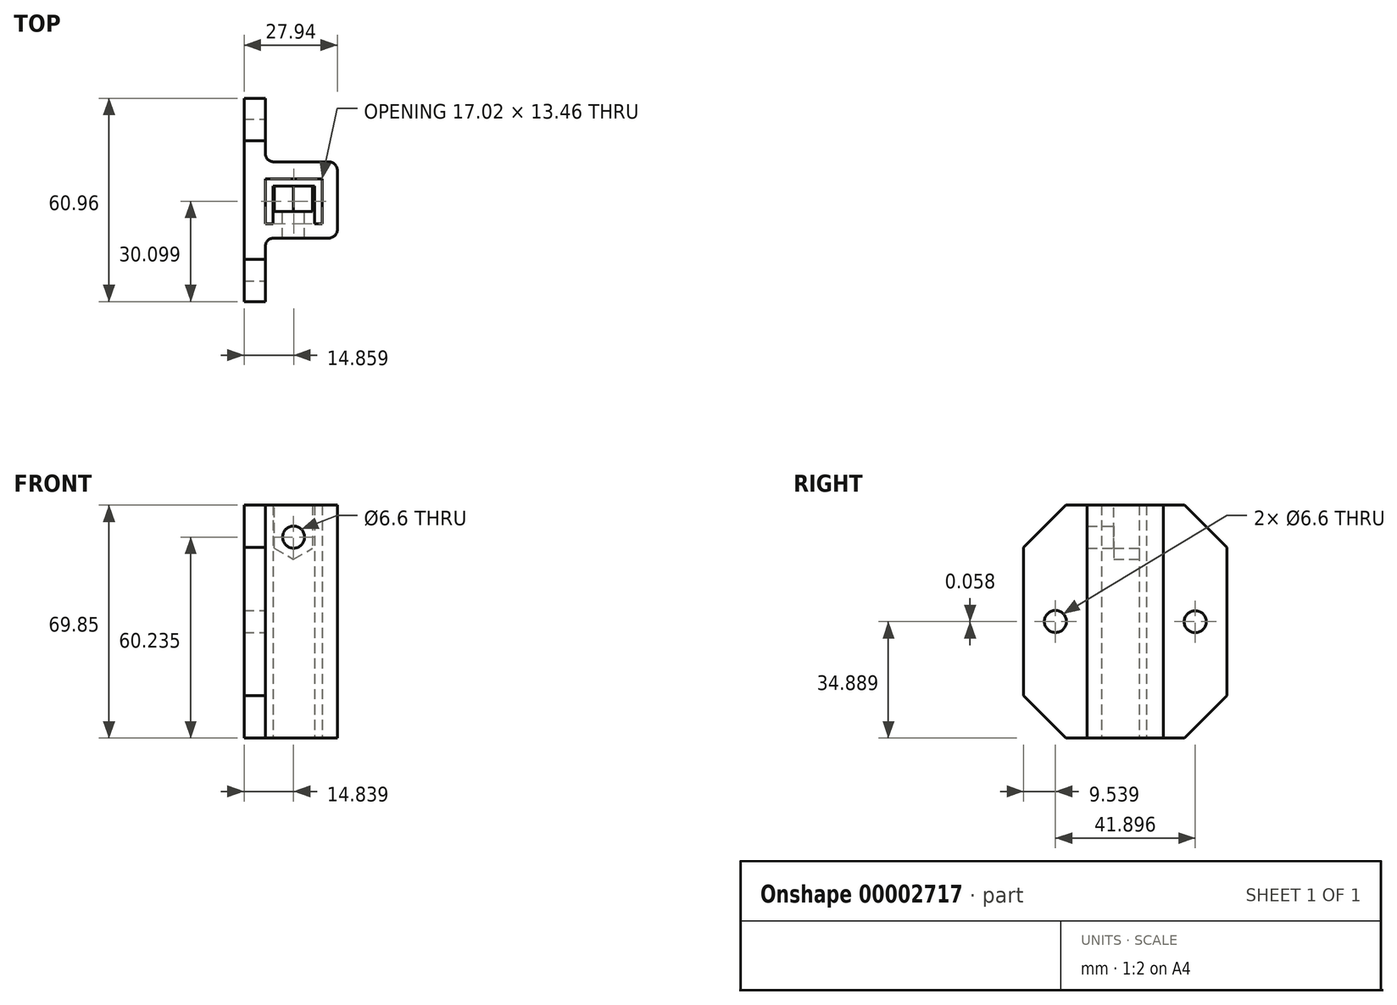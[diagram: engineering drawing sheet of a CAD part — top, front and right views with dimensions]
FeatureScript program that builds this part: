
annotation { "Feature Type Name" : "Feature", "Feature Type Description" : "" }
export const myFeature = defineFeature(function(context is Context, id is Id, definition is map)
    precondition{}
    {
        {
            var Q0;
            Q0=qCreatedBy(makeId("Top.planeOp"),FACE);
            var sketch = newSketch(context, id + "F0", { "sketchPlane" : qUnion([Q0])});
            skLineSegment(sketch, "E0", {"start": v(0, 0) * mm, "end": v(17.02, 0) * mm});
            skLineSegment(sketch, "E1", {"start": v(17.02, 0) * mm, "end": v(17.02, -13.46) * mm});
            skLineSegment(sketch, "E2", {"start": v(17.02, -13.46) * mm, "end": v(14.73, -13.46) * mm});
            skLineSegment(sketch, "E3", {"start": v(14.73, -13.46) * mm, "end": v(14.73, -2.18) * mm});
            skLineSegment(sketch, "E4", {"start": v(14.73, -2.18) * mm, "end": v(2.29, -2.18) * mm});
            skLineSegment(sketch, "E5", {"start": v(2.29, -2.18) * mm, "end": v(2.29, -13.46) * mm});
            skLineSegment(sketch, "E6", {"start": v(2.29, -13.46) * mm, "end": v(0, -13.46) * mm});
            skLineSegment(sketch, "E7", {"start": v(0, -13.46) * mm, "end": v(0, 0) * mm});
            skSolve(sketch);
        }
        {
            var Q0;
            Q0=qCreatedBy(makeId("Top.planeOp"),FACE);
            var sketch = newSketch(context, id + "F1", { "sketchPlane" : qUnion([Q0])});
            skLineSegment(sketch, "E8.bottom", {"start": v(0, 0) * mm, "end": v(26.67, 0) * mm});
            skLineSegment(sketch, "E8.top", {"start": v(0, -22.86) * mm, "end": v(26.67, -22.86) * mm});
            skLineSegment(sketch, "E8.left", {"start": v(0, 0) * mm, "end": v(0, -22.86) * mm});
            skLineSegment(sketch, "E8.right", {"start": v(26.67, 0) * mm, "end": v(26.67, -22.86) * mm});
            skSolve(sketch);
        }
        {
            var Q0;
            Q0=makeQuery(id+"F1.imprint","IMPRINT",FACE,{"disambiguationData":[TD([[makeQuery(id+"F1.imprint","IMPRINT",EDGE,{"derivedFrom":sQuery(id+"F1.wireOp",EDGE,"E8.bottom")}),-1.0]])]});
            extrude(context, id + "F2", {"entities" : qUnion([Q0]), "depth" : 69.85 * mm});
        }
        {
            var Q0;
            Q0=makeQuery(id+"F2.opExtrude","SWEPT_BODY",BODY,{"disambiguationData":[OSD([sQuery(id+"F1.wireOp",EDGE,"E8.bottom"),sQuery(id+"F1.wireOp",EDGE,"E8.top"),sQuery(id+"F1.wireOp",EDGE,"E8.left"),sQuery(id+"F1.wireOp",EDGE,"E8.right")])]});
            transform(context, id + "F3", {"entities" : qUnion([Q0]), "transformType" : TransformType.TRANSLATION_3D, "dx" : 0 * mm, "dy" : 5.08 * mm, "dz" : 0 * mm, "makeCopy" : false});
        }
        {
            var Q0;
            Q0=qCreatedBy(makeId("Top.planeOp"),FACE);
            var sketch = newSketch(context, id + "F4", { "sketchPlane" : qUnion([Q0])});
            skLineSegment(sketch, "E9", {"start": v(0, 0) * mm, "end": v(-5.08, 0) * mm});
            skSolve(sketch);
        }
        {
            var Q0;
            Q0=makeQuery(id+"F2.opExtrude","SWEPT_BODY",BODY,{"disambiguationData":[OSD([sQuery(id+"F1.wireOp",EDGE,"E8.bottom"),sQuery(id+"F1.wireOp",EDGE,"E8.top"),sQuery(id+"F1.wireOp",EDGE,"E8.left"),sQuery(id+"F1.wireOp",EDGE,"E8.right")])]});
            var Q1;
            Q1=sQuery(id+"F4.wireOp",EDGE,"E9");
            transform(context, id + "F5", {"entities" : qUnion([Q0]), "transformType" : TransformType.TRANSLATION_ENTITY, "oppositeDirectionEntity" : false, "transformLine" : qUnion([Q1]), "makeCopy" : false});
        }
        {
            var Q0;
            Q0=makeQuery(id+"F0.imprint","IMPRINT",FACE,{"disambiguationData":[TD([[makeQuery(id+"F0.imprint","IMPRINT",EDGE,{"derivedFrom":sQuery(id+"F0.wireOp",EDGE,"E0")}),-1.0]])]});
            extrude(context, id + "F6", {"entities" : qUnion([Q0]), "operationType" : NewBodyOperationType.REMOVE, "depth" : 71.12 * mm});
        }
        {
            var Q0;
            Q0=qCreatedBy(makeId("Top.planeOp"),FACE);
            var sketch = newSketch(context, id + "F7", { "sketchPlane" : qUnion([Q0])});
            skLineSegment(sketch, "E10", {"start": v(0, 0) * mm, "end": v(0, 24.13) * mm});
            skLineSegment(sketch, "E11", {"start": v(0, 24.13) * mm, "end": v(-6.35, 24.13) * mm});
            skLineSegment(sketch, "E12", {"start": v(-6.35, 24.13) * mm, "end": v(-6.35, -36.83) * mm});
            skLineSegment(sketch, "E13", {"start": v(-6.35, -36.83) * mm, "end": v(0, -36.83) * mm});
            skLineSegment(sketch, "E14", {"start": v(0, -36.83) * mm, "end": v(0, 0) * mm});
            skSolve(sketch);
        }
        {
            var Q0;
            Q0=makeQuery(id+"F7.imprint","IMPRINT",FACE,{"disambiguationData":[TD([[makeQuery(id+"F7.imprint","IMPRINT",EDGE,{"derivedFrom":sQuery(id+"F7.wireOp",EDGE,"E11")}),1.0]])]});
            extrude(context, id + "F8", {"entities" : qUnion([Q0]), "operationType" : NewBodyOperationType.ADD, "depth" : 69.85 * mm});
        }
        {
            var Q0;
            Q0=makeQuery(id+"F8.opExtrude","CAP_EDGE",EDGE,{"disambiguationData":[OSD([sQuery(id+"F7.wireOp",EDGE,"E13")])],"isStart":true});
            var Q1;
            Q1=makeQuery(id+"F8.opExtrude","CAP_EDGE",EDGE,{"disambiguationData":[OSD([sQuery(id+"F7.wireOp",EDGE,"E13")])],"isStart":false});
            var Q2;
            Q2=makeQuery(id+"F8.opExtrude","CAP_EDGE",EDGE,{"disambiguationData":[OSD([sQuery(id+"F7.wireOp",EDGE,"E11")])],"isStart":false});
            var Q3;
            Q3=makeQuery(id+"F8.opExtrude","CAP_EDGE",EDGE,{"disambiguationData":[OSD([sQuery(id+"F7.wireOp",EDGE,"E11")])],"isStart":true});
            chamfer(context, id + "F9", {"entities" : qUnion([Q0, Q1, Q2, Q3]), "width" : 12.7 * mm, "tangentPropagation" : true});
        }
        {
            var Q0;
            Q0=qCreatedBy(makeId("Top.planeOp"),FACE);
            cPlane(context, id + "F10", {"entities" : qUnion([Q0]), "cplaneType" : CPlaneType.OFFSET, "offset" : 34.92 * mm, "width" : 152.4 * mm, "height" : 152.4 * mm});
        }
        {
            var Q0;
            Q0=qCreatedBy(makeId("Right.planeOp"),FACE);
            var sketch = newSketch(context, id + "F11", { "sketchPlane" : qUnion([Q0])});
            skCircle(sketch, "E15", {"center": v(14.6, 34.89) * mm, "radius": 3.3 * mm});
            skCircle(sketch, "E16", {"center": v(-27.3, 34.95) * mm, "radius": 3.3 * mm});
            skLineSegment(sketch, "E17", {"start": v(14.6, 34.89) * mm, "end": v(-27.3, 34.89) * mm});
            skSolve(sketch);
        }
        {
            var Q0;
            {var subQ1=sQuery(id+"F11.wireOp",EDGE,"E15");var subQ2=sQuery(id+"F11.wireOp",EDGE,"E16");Q0=qUnion([makeQuery(id+"F11.imprint","IMPRINT",FACE,{"disambiguationData":[TD([[makeQuery(id+"F11.imprint","IMPRINT",EDGE,{"derivedFrom":subQ1}),1.0]])]}),makeQuery(id+"F11.imprint","IMPRINT",FACE,{"disambiguationData":[TD([[makeQuery(id+"F11.imprint","IMPRINT",EDGE,{"derivedFrom":subQ2}),1.0]])]})]);}
            extrude(context, id + "F12", {"entities" : qUnion([Q0]), "operationType" : NewBodyOperationType.REMOVE, "oppositeDirection" : true, "depth" : 25.4 * mm});
        }
        {
            var Q0;
            Q0=makeQuery(id+"F2.opExtrude","SWEPT_EDGE",EDGE,{"disambiguationData":[OSD([sQuery(id+"F1.wireOp",EDGE,"E8.top"),sQuery(id+"F1.wireOp",EDGE,"E8.right")])]});
            var Q1;
            Q1=makeQuery(id+"F2.opExtrude","SWEPT_EDGE",EDGE,{"disambiguationData":[OSD([sQuery(id+"F1.wireOp",EDGE,"E8.bottom"),sQuery(id+"F1.wireOp",EDGE,"E8.right")])]});
            var Q2;
            Q2=makeQuery(id+"F8.boolean.opBoolean","INTERSECT",EDGE,{"derivedFrom":[makeQuery(id+"F2.opExtrude","SWEPT_FACE",FACE,{"disambiguationData":[OSD([sQuery(id+"F1.wireOp",EDGE,"E8.bottom")])]}),makeQuery(id+"F8.opExtrude","SWEPT_FACE",FACE,{"disambiguationData":[OSD([sQuery(id+"F7.wireOp",EDGE,"E14")])]})]});
            var Q3;
            Q3=makeQuery(id+"F8.boolean.opBoolean","INTERSECT",EDGE,{"derivedFrom":[makeQuery(id+"F2.opExtrude","SWEPT_FACE",FACE,{"disambiguationData":[OSD([sQuery(id+"F1.wireOp",EDGE,"E8.top")])]}),makeQuery(id+"F8.opExtrude","SWEPT_FACE",FACE,{"disambiguationData":[OSD([sQuery(id+"F7.wireOp",EDGE,"E14")])]})]});
            fillet(context, id + "F13", {"entities" : qUnion([Q0, Q1, Q2, Q3]), "radius" : 2.54 * mm, "tangentPropagation" : true, "allowEdgeOverflow" : false});
        }
        {
            var Q0;
            Q0=qCreatedBy(makeId("Front.planeOp"),FACE);
            var sketch = newSketch(context, id + "F14", { "sketchPlane" : qUnion([Q0])});
            skCircle(sketch, "E18", {"center": v(8.49, 60.23) * mm, "radius": 3.3 * mm});
            skSolve(sketch);
        }
        {
            var Q0;
            Q0=makeQuery(id+"F14.imprint","IMPRINT",FACE,{"disambiguationData":[TD([[makeQuery(id+"F14.imprint","IMPRINT",EDGE,{"derivedFrom":sQuery(id+"F14.wireOp",EDGE,"E18")}),1.0]])]});
            extrude(context, id + "F15", {"entities" : qUnion([Q0]), "operationType" : NewBodyOperationType.REMOVE, "depth" : 25.4 * mm});
        }
        {
            var Q0;
            Q0=makeQuery(id+"F6.boolean.opBoolean","COPY",FACE,{"derivedFrom":makeQuery(id+"F6.opExtrude","SWEPT_FACE",FACE,{"disambiguationData":[OSD([sQuery(id+"F0.wireOp",EDGE,"E4")])]})});
            var sketch = newSketch(context, id + "F16", { "sketchPlane" : qUnion([Q0])});
            skLineSegment(sketch, "E19", {"start": v(-8.49, 60.23) * mm, "end": v(-14.2, 60.23) * mm});
            skCircle(sketch, "E20.cCircle", {"center": v(-8.49, 60.23) * mm, "radius": 5.72 * mm, "construction": true});
            skLineSegment(sketch, "E20.0", {"start": v(-14.2, 56.94) * mm, "end": v(-14.2, 63.53) * mm});
            skLineSegment(sketch, "E20.1", {"start": v(-14.2, 63.53) * mm, "end": v(-8.49, 66.83) * mm});
            skLineSegment(sketch, "E20.2", {"start": v(-8.49, 66.83) * mm, "end": v(-2.77, 63.53) * mm});
            skLineSegment(sketch, "E20.3", {"start": v(-2.77, 63.53) * mm, "end": v(-2.77, 56.94) * mm});
            skLineSegment(sketch, "E20.4", {"start": v(-2.77, 56.94) * mm, "end": v(-8.49, 53.64) * mm});
            skLineSegment(sketch, "E20.5", {"start": v(-8.49, 53.64) * mm, "end": v(-14.2, 56.94) * mm});
            skPoint(sketch, "E20.0.midPoint", {"position": v(-14.2, 60.23) * mm});
            skLineSegment(sketch, "E21", {"start": v(-2.77, 63.53) * mm, "end": v(-2.77, 69.85) * mm});
            skLineSegment(sketch, "E22", {"start": v(-2.77, 69.85) * mm, "end": v(-14.2, 69.85) * mm});
            skLineSegment(sketch, "E23", {"start": v(-14.2, 69.85) * mm, "end": v(-14.2, 63.53) * mm});
            skSolve(sketch);
        }
        {
            var Q0;
            {var subQ0=makeQuery(id+"F15.boolean.opBoolean","INTERSECT",EDGE,{"derivedFrom":[makeQuery(id+"F6.boolean.opBoolean","COPY",FACE,{"derivedFrom":makeQuery(id+"F6.opExtrude","SWEPT_FACE",FACE,{"disambiguationData":[OSD([sQuery(id+"F0.wireOp",EDGE,"E4")])]})}),makeQuery(id+"F15.opExtrude","SWEPT_FACE",FACE,{"disambiguationData":[OSD([sQuery(id+"F14.wireOp",EDGE,"E18")])]})]});var subQ1=makeQuery(id+"F16.imprint","IMPRINT",EDGE,{"derivedFrom":subQ0});var subQ6=sQuery(id+"F16.wireOp",EDGE,"E20.1");var subQ7=makeQuery(id+"F16.imprint","IMPRINT",EDGE,{"derivedFrom":subQ6});Q0=qUnion([makeQuery(id+"F16.imprint","IMPRINT",FACE,{"disambiguationData":[TD([[subQ1,1.0]])]}),makeQuery(id+"F16.imprint","IMPRINT",FACE,{"disambiguationData":[TD([[subQ7,1.0]])]}),makeQuery(id+"F16.imprint","IMPRINT",FACE,{"disambiguationData":[TD([[subQ7,-1.0]])]})]);}
            extrude(context, id + "F17", {"entities" : qUnion([Q0]), "operationType" : NewBodyOperationType.REMOVE, "oppositeDirection" : true, "depth" : 7.62 * mm});
        }
    });
